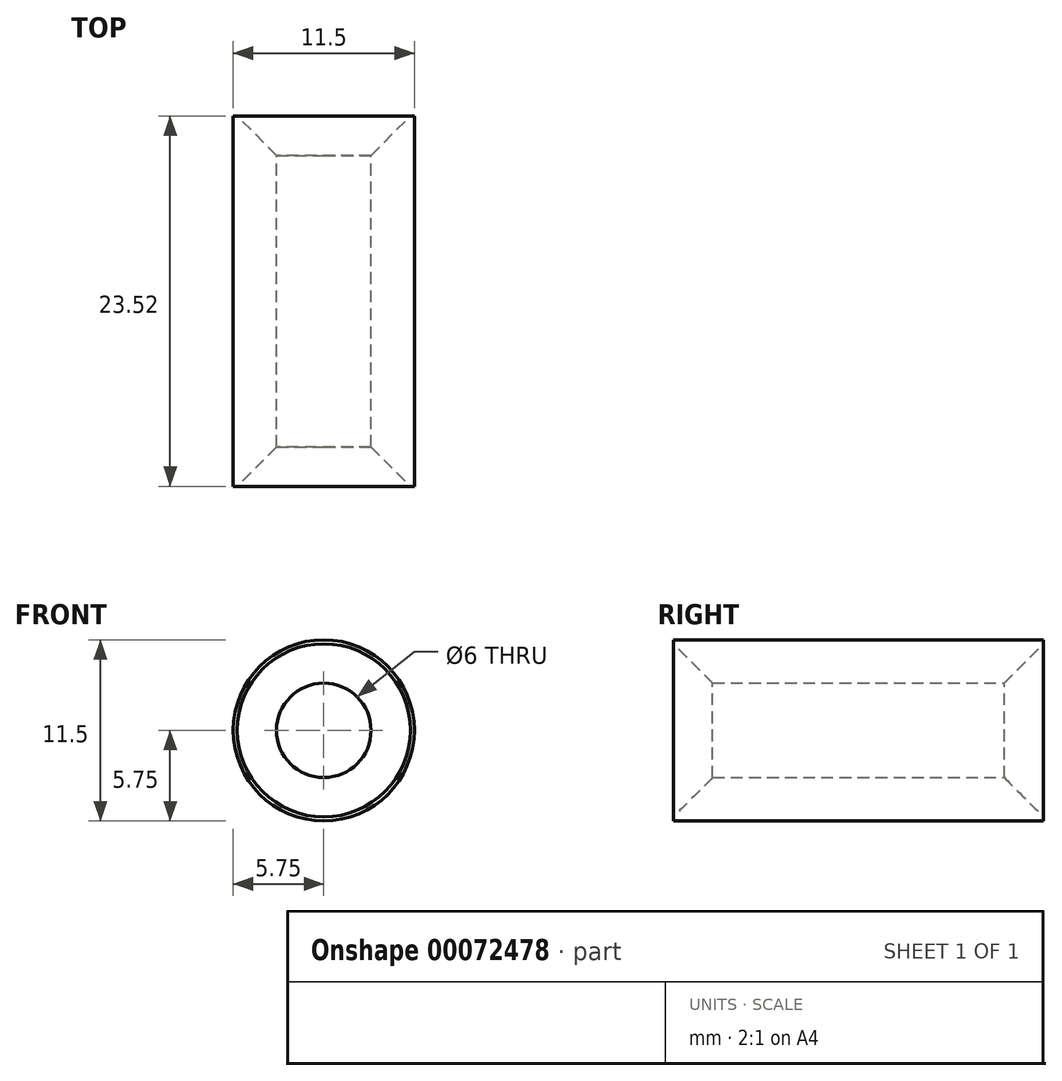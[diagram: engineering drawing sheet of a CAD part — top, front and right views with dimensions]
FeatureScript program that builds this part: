
annotation { "Feature Type Name" : "Feature", "Feature Type Description" : "" }
export const myFeature = defineFeature(function(context is Context, id is Id, definition is map)
    precondition{}
    {
        {
            var Q0;
            Q0=qCreatedBy(makeId("Front.planeOp"),FACE);
            var sketch = newSketch(context, id + "F0", { "sketchPlane" : qUnion([Q0])});
            skCircle(sketch, "E0", {"center": v(0, 0) * mm, "radius": 5.75 * mm});
            skCircle(sketch, "E1", {"center": v(0, 0) * mm, "radius": 3 * mm});
            skSolve(sketch);
        }
        {
            var Q0;
            Q0=makeQuery(id+"F0.imprint","IMPRINT",FACE,{"disambiguationData":[TD([[makeQuery(id+"F0.imprint","IMPRINT",EDGE,{"derivedFrom":sQuery(id+"F0.wireOp",EDGE,"E0")}),1.0]])]});
            extrude(context, id + "F1", {"entities" : qUnion([Q0]), "depth" : 23.52 * mm});
        }
        {
            var Q0;
            Q0=makeQuery(id+"F1.opExtrude","SWEPT_FACE",FACE,{"disambiguationData":[OSD([sQuery(id+"F0.wireOp",EDGE,"E1")])]});
            chamfer(context, id + "F2", {"entities" : qUnion([Q0]), "width" : 2.5 * mm, "tangentPropagation" : true});
        }
    });
